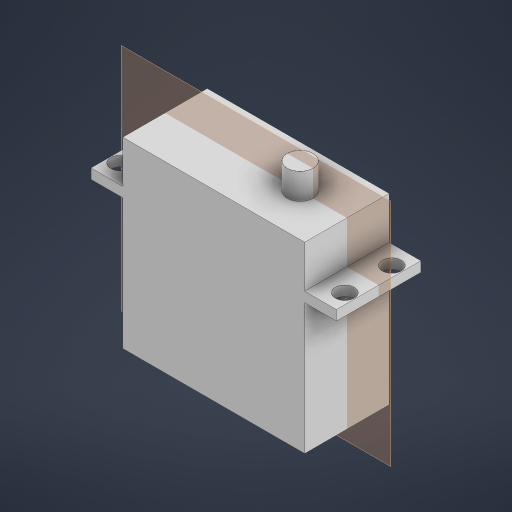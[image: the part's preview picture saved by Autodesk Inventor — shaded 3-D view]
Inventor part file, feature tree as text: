
AUTODESK INVENTOR PART (.ipt)
format: ipt  version: 2024 (Build 280153000, 153)  size: 217,600 bytes
history: native  units: in
note: dims shown in document units (in); Inventor stores cm internally (conversion verified against a paired STEP export)
features: extrude x4, sketch x4, projected_geometry x2, plane x1
ambient origin geometry x8: Origin, YZ Plane, XZ Plane, XY Plane, X Axis, Y Axis, Z Axis, Center Point
bodies: Solid1 (feature_tree)
feature tree (11):
  extrude  "Extrusion1"  Depth=1.1417in
  extrude  "Extrusion2"  Depth=2.1449in
  extrude  "Extrusion3"  Depth=0.1634in
  extrude  "Extrusion4"  Depth=0.0874in TaperAngle=0.0deg
  plane  "Work Plane1"
  sketch  "Sketch2"  dims[d0=1.5902in d1=1.1417in]
  sketch  "Sketch3"  dims[d2=0.7382in d3=0.0in d4=2.1449in]
  projected_geometry  "Projected Loop1"
  sketch  "Sketch4"  dims[d5=0.1654in d6=0.1634in]
  sketch  "Sketch5"  dims[d7=0.187in d8=0.0874in d9=0.0in d10=0.3709in d11=0.0in d12=1.1811in d13=0.2256in d14=0.2272in d15=0.0in]
  projected_geometry  "Projected Loop2"
